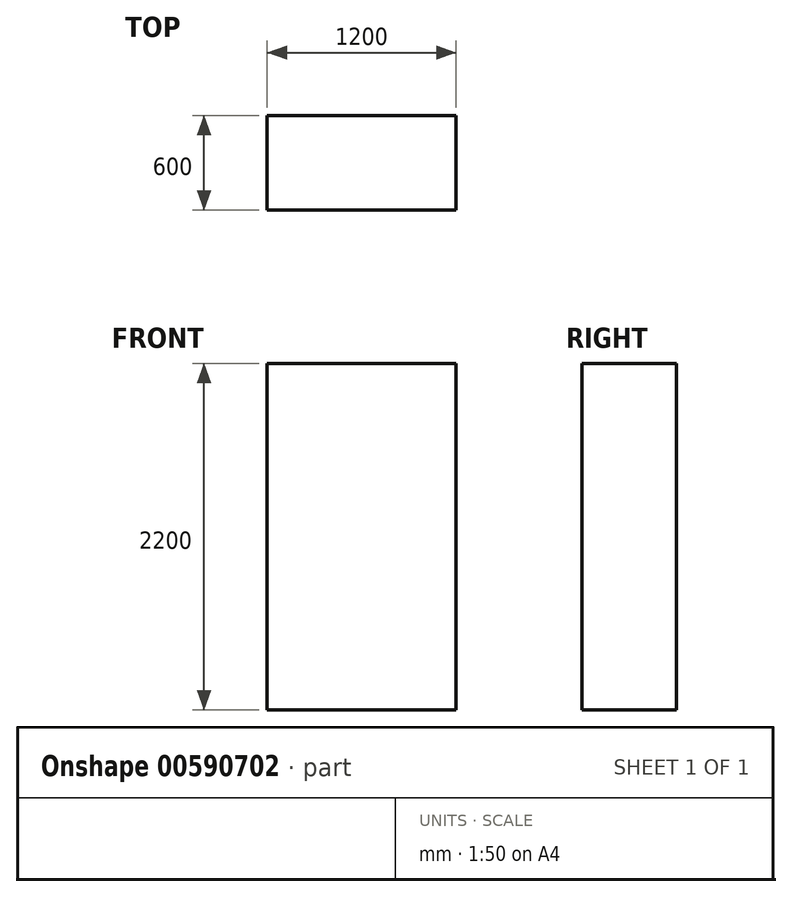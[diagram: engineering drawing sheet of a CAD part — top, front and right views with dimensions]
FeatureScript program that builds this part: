
annotation { "Feature Type Name" : "Feature", "Feature Type Description" : "" }
export const myFeature = defineFeature(function(context is Context, id is Id, definition is map)
    precondition{}
    {
        {
            var Q0;
            Q0=qCreatedBy(makeId("Front.planeOp"),FACE);
            var sketch = newSketch(context, id + "F0", { "sketchPlane" : qUnion([Q0])});
            skLineSegment(sketch, "E0.bottom", {"start": v(-600, 1100) * mm, "end": v(600, 1100) * mm});
            skLineSegment(sketch, "E0.top", {"start": v(-600, -1100) * mm, "end": v(600, -1100) * mm});
            skLineSegment(sketch, "E0.left", {"start": v(-600, 1100) * mm, "end": v(-600, -1100) * mm});
            skLineSegment(sketch, "E0.right", {"start": v(600, 1100) * mm, "end": v(600, -1100) * mm});
            skPoint(sketch, "E0.middle", {"position": v(0, 0) * mm});
            skSolve(sketch);
        }
        {
            var Q0;
            Q0=makeQuery(id+"F0.imprint","IMPRINT",FACE,{"disambiguationData":[TD([[makeQuery(id+"F0.imprint","IMPRINT",EDGE,{"derivedFrom":sQuery(id+"F0.wireOp",EDGE,"E0.bottom")}),-1.0]])]});
            extrude(context, id + "F1", {"entities" : qUnion([Q0]), "depth" : 600 * mm, "offsetDistance" : 25 * mm});
        }
    });
